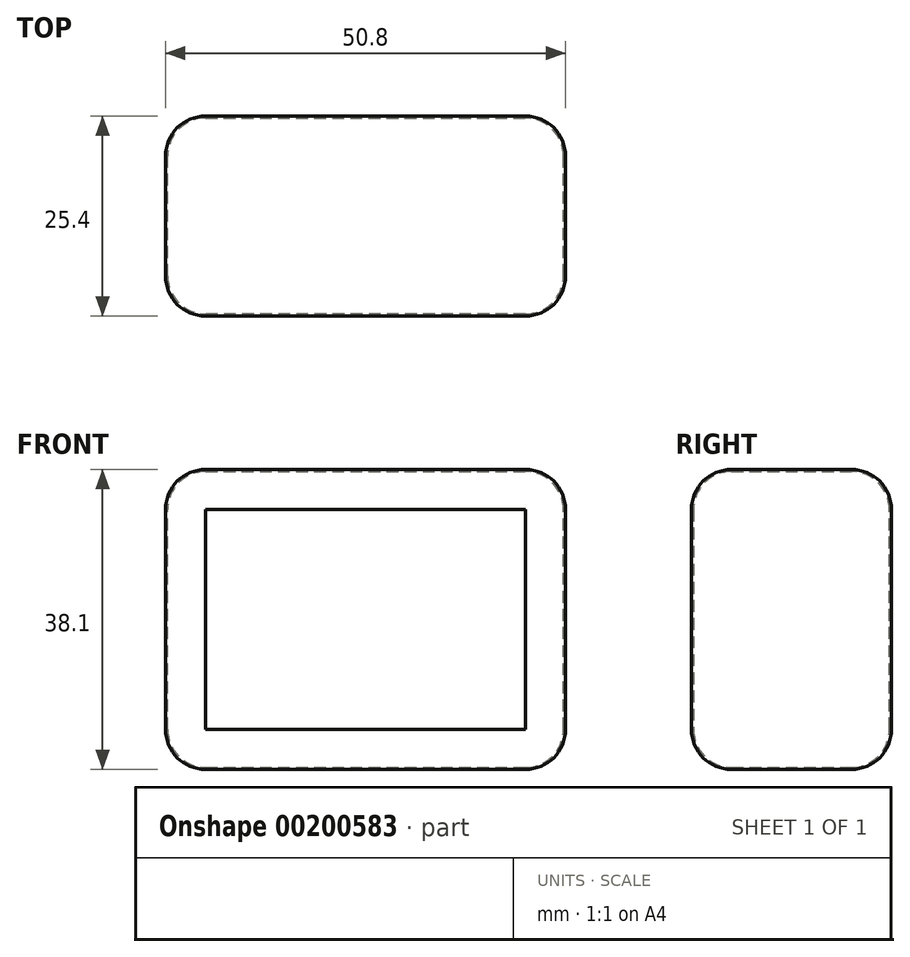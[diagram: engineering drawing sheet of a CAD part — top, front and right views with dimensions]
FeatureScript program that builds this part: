
annotation { "Feature Type Name" : "Feature", "Feature Type Description" : "" }
export const myFeature = defineFeature(function(context is Context, id is Id, definition is map)
    precondition{}
    {
        {
            var Q0;
            Q0=qCreatedBy(makeId("Front.planeOp"),FACE);
            var sketch = newSketch(context, id + "F0", { "sketchPlane" : qUnion([Q0])});
            skLineSegment(sketch, "E0.bottom", {"start": v(0, 0) * mm, "end": v(50.8, 0) * mm});
            skLineSegment(sketch, "E0.top", {"start": v(0, 38.1) * mm, "end": v(50.8, 38.1) * mm});
            skLineSegment(sketch, "E0.left", {"start": v(0, 0) * mm, "end": v(0, 38.1) * mm});
            skLineSegment(sketch, "E0.right", {"start": v(50.8, 0) * mm, "end": v(50.8, 38.1) * mm});
            skSolve(sketch);
        }
        {
            var Q0;
            Q0=makeQuery(id+"F0.imprint","IMPRINT",FACE,{"disambiguationData":[TD([[makeQuery(id+"F0.imprint","IMPRINT",EDGE,{"derivedFrom":sQuery(id+"F0.wireOp",EDGE,"E0.bottom")}),1.0]])]});
            extrude(context, id + "F1", {"entities" : qUnion([Q0]), "depth" : 25.4 * mm});
        }
        {
            var Q0;
            Q0=makeQuery(id+"F1.opExtrude","SWEPT_EDGE",EDGE,{"disambiguationData":[OSD([sQuery(id+"F0.wireOp",EDGE,"E0.top"),sQuery(id+"F0.wireOp",EDGE,"E0.right")])]});
            var Q1;
            Q1=makeQuery(id+"F1.opExtrude","CAP_EDGE",EDGE,{"disambiguationData":[OSD([sQuery(id+"F0.wireOp",EDGE,"E0.top")])],"isStart":false});
            var Q2;
            Q2=makeQuery(id+"F1.opExtrude","CAP_EDGE",EDGE,{"disambiguationData":[OSD([sQuery(id+"F0.wireOp",EDGE,"E0.top")])],"isStart":true});
            var Q3;
            Q3=makeQuery(id+"F1.opExtrude","CAP_EDGE",EDGE,{"disambiguationData":[OSD([sQuery(id+"F0.wireOp",EDGE,"E0.right")])],"isStart":false});
            var Q4;
            Q4=makeQuery(id+"F1.opExtrude","CAP_EDGE",EDGE,{"disambiguationData":[OSD([sQuery(id+"F0.wireOp",EDGE,"E0.right")])],"isStart":true});
            var Q5;
            Q5=makeQuery(id+"F1.opExtrude","SWEPT_EDGE",EDGE,{"disambiguationData":[OSD([sQuery(id+"F0.wireOp",EDGE,"E0.bottom"),sQuery(id+"F0.wireOp",EDGE,"E0.right")])]});
            var Q6;
            Q6=makeQuery(id+"F1.opExtrude","CAP_EDGE",EDGE,{"disambiguationData":[OSD([sQuery(id+"F0.wireOp",EDGE,"E0.bottom")])],"isStart":false});
            var Q7;
            Q7=makeQuery(id+"F1.opExtrude","CAP_EDGE",EDGE,{"disambiguationData":[OSD([sQuery(id+"F0.wireOp",EDGE,"E0.bottom")])],"isStart":true});
            var Q8;
            Q8=makeQuery(id+"F1.opExtrude","CAP_EDGE",EDGE,{"disambiguationData":[OSD([sQuery(id+"F0.wireOp",EDGE,"E0.left")])],"isStart":false});
            var Q9;
            Q9=makeQuery(id+"F1.opExtrude","SWEPT_EDGE",EDGE,{"disambiguationData":[OSD([sQuery(id+"F0.wireOp",EDGE,"E0.top"),sQuery(id+"F0.wireOp",EDGE,"E0.left")])]});
            var Q10;
            Q10=makeQuery(id+"F1.opExtrude","SWEPT_EDGE",EDGE,{"disambiguationData":[OSD([sQuery(id+"F0.wireOp",EDGE,"E0.bottom"),sQuery(id+"F0.wireOp",EDGE,"E0.left")])]});
            var Q11;
            Q11=makeQuery(id+"F1.opExtrude","CAP_EDGE",EDGE,{"disambiguationData":[OSD([sQuery(id+"F0.wireOp",EDGE,"E0.left")])],"isStart":true});
            fillet(context, id + "F2", {"entities" : qUnion([Q0, Q1, Q2, Q3, Q4, Q5, Q6, Q7, Q8, Q9, Q10, Q11]), "radius" : 5.08 * mm, "tangentPropagation" : true, "allowEdgeOverflow" : false});
        }
        {
            var Q0;
            Q0=makeQuery(id+"F1.opExtrude","CAP_FACE",FACE,{"disambiguationData":[OSD([sQuery(id+"F0.wireOp",EDGE,"E0.bottom"),sQuery(id+"F0.wireOp",EDGE,"E0.top"),sQuery(id+"F0.wireOp",EDGE,"E0.left"),sQuery(id+"F0.wireOp",EDGE,"E0.right")])],"isStart":false});
            shell(context, id + "F3", {"entities" : qUnion([Q0]), "thickness" : 0.25 * mm});
        }
    });
